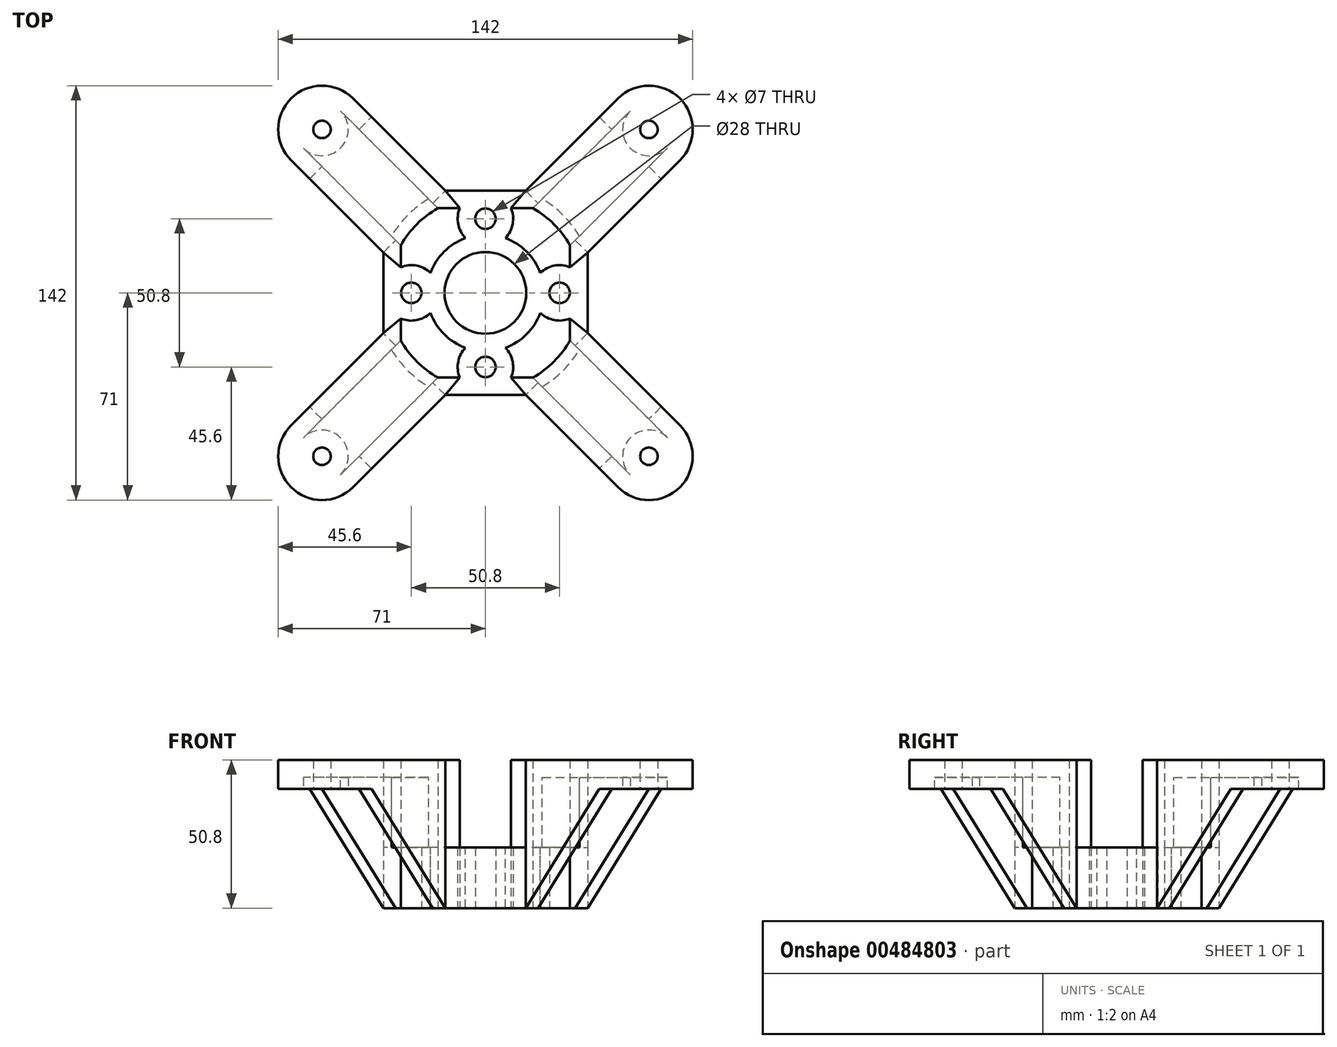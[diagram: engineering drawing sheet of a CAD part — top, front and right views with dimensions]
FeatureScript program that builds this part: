
annotation { "Feature Type Name" : "Feature", "Feature Type Description" : "" }
export const myFeature = defineFeature(function(context is Context, id is Id, definition is map)
    precondition{}
    {
        {
            var Q0;
            Q0=qCreatedBy(makeId("Top.planeOp"),FACE);
            var sketch = newSketch(context, id + "F0", { "sketchPlane" : qUnion([Q0])});
            skCircle(sketch, "E0", {"center": v(0, 0) * mm, "radius": 14 * mm});
            skCircle(sketch, "E1", {"center": v(0, 0) * mm, "radius": 25.4 * mm});
            skLineSegment(sketch, "E2", {"start": v(0, 0) * mm, "end": v(0, 25.4) * mm, "construction": true});
            skLineSegment(sketch, "E3", {"start": v(0, 0) * mm, "end": v(0, -25.4) * mm, "construction": true});
            skCircle(sketch, "E4", {"center": v(0, 25.4) * mm, "radius": 3.5 * mm});
            skLineSegment(sketch, "E5", {"start": v(0, 0) * mm, "end": v(25.4, 0) * mm, "construction": true});
            skCircle(sketch, "E6.MirrorC", {"center": v(0, -25.4) * mm, "radius": 3.5 * mm});
            skLineSegment(sketch, "E7.bottom", {"start": v(-35, 35) * mm, "end": v(35, 35) * mm});
            skLineSegment(sketch, "E7.top", {"start": v(-35, -35) * mm, "end": v(35, -35) * mm});
            skLineSegment(sketch, "E7.left", {"start": v(-35, 35) * mm, "end": v(-35, -35) * mm});
            skLineSegment(sketch, "E7.right", {"start": v(35, 35) * mm, "end": v(35, -35) * mm});
            skCircle(sketch, "E8", {"center": v(25.4, 0) * mm, "radius": 3.5 * mm});
            skCircle(sketch, "E9.MirrorC", {"center": v(-25.4, 0) * mm, "radius": 3.5 * mm});
            skLineSegment(sketch, "E10.bottom", {"start": v(-56, -56) * mm, "end": v(56, -56) * mm, "construction": true});
            skLineSegment(sketch, "E10.top", {"start": v(-56, 56) * mm, "end": v(56, 56) * mm, "construction": true});
            skLineSegment(sketch, "E10.left", {"start": v(-56, -56) * mm, "end": v(-56, 56) * mm, "construction": true});
            skLineSegment(sketch, "E10.right", {"start": v(56, -56) * mm, "end": v(56, 56) * mm, "construction": true});
            skLineSegment(sketch, "E11", {"start": v(0, 0) * mm, "end": v(-56, 56) * mm, "construction": true});
            skLineSegment(sketch, "E12.0", {"start": v(-13.79, 35) * mm, "end": v(-45.4, 66.6) * mm});
            skLineSegment(sketch, "E13.0", {"start": v(-35, 13.79) * mm, "end": v(-66.6, 45.4) * mm});
            skArc(sketch, "E14", {"start": v(-45.4, 66.6) * mm, "mid": v(-66.6, 66.6) * mm, "end": v(-66.6, 45.4) * mm});
            skCircle(sketch, "E15", {"center": v(-56, 56) * mm, "radius": 3 * mm});
            skLineSegment(sketch, "E16.MirrorCS", {"start": v(13.79, 35) * mm, "end": v(45.4, 66.6) * mm});
            skArc(sketch, "E17.MirrorCS", {"start": v(45.4, 66.6) * mm, "mid": v(66.6, 66.6) * mm, "end": v(66.6, 45.4) * mm});
            skLineSegment(sketch, "E18.MirrorCS", {"start": v(35, 13.79) * mm, "end": v(66.6, 45.4) * mm});
            skCircle(sketch, "E19.MirrorC", {"center": v(56, 56) * mm, "radius": 3 * mm});
            skLineSegment(sketch, "E20.MirrorCS", {"start": v(-13.79, -35) * mm, "end": v(-45.4, -66.6) * mm});
            skArc(sketch, "E21.MirrorCS", {"start": v(-45.4, -66.6) * mm, "mid": v(-66.6, -66.6) * mm, "end": v(-66.6, -45.4) * mm});
            skLineSegment(sketch, "E22.MirrorCS", {"start": v(-35, -13.79) * mm, "end": v(-66.6, -45.4) * mm});
            skCircle(sketch, "E23.MirrorC", {"center": v(-56, -56) * mm, "radius": 3 * mm});
            skCircle(sketch, "E24.MirrorC", {"center": v(56, -56) * mm, "radius": 3 * mm});
            skArc(sketch, "E25.MirrorCS", {"start": v(45.4, -66.6) * mm, "mid": v(66.6, -66.6) * mm, "end": v(66.6, -45.4) * mm});
            skLineSegment(sketch, "E26.MirrorCS", {"start": v(13.79, -35) * mm, "end": v(45.4, -66.6) * mm});
            skLineSegment(sketch, "E27.MirrorCS", {"start": v(35, -13.79) * mm, "end": v(66.6, -45.4) * mm});
            skSolve(sketch);
        }
        {
            var Q0;
            Q0 = qSketchRegion(id + "F0", true);
            var Q1;
            Q1=makeQuery(id+"F0.imprint","IMPRINT",FACE,{"disambiguationData":[TD([[makeQuery(id+"F0.imprint","IMPRINT",EDGE,{"derivedFrom":sQuery(id+"F0.wireOp",EDGE,"E0")}),-1.0]])]});
            extrude(context, id + "F1", {"entities" : qUnion([Q0, Q1]), "depth" : 50.8 * mm});
        }
        {
            var Q0;
            Q0=makeQuery(id+"F1.opExtrude","CAP_FACE",FACE,{"disambiguationData":[OSD([sQuery(id+"F0.wireOp",EDGE,"E0"),sQuery(id+"F0.wireOp",EDGE,"E4"),sQuery(id+"F0.wireOp",EDGE,"E6.MirrorC"),sQuery(id+"F0.wireOp",EDGE,"E7.bottom"),sQuery(id+"F0.wireOp",EDGE,"E7.top"),sQuery(id+"F0.wireOp",EDGE,"E7.left"),sQuery(id+"F0.wireOp",EDGE,"E7.right"),sQuery(id+"F0.wireOp",EDGE,"E8"),sQuery(id+"F0.wireOp",EDGE,"E9.MirrorC"),sQuery(id+"F0.wireOp",EDGE,"E12.0"),sQuery(id+"F0.wireOp",EDGE,"E13.0"),sQuery(id+"F0.wireOp",EDGE,"E14"),sQuery(id+"F0.wireOp",EDGE,"E15"),sQuery(id+"F0.wireOp",EDGE,"E16.MirrorCS"),sQuery(id+"F0.wireOp",EDGE,"E17.MirrorCS"),sQuery(id+"F0.wireOp",EDGE,"E18.MirrorCS"),sQuery(id+"F0.wireOp",EDGE,"E19.MirrorC"),sQuery(id+"F0.wireOp",EDGE,"E20.MirrorCS"),sQuery(id+"F0.wireOp",EDGE,"E21.MirrorCS"),sQuery(id+"F0.wireOp",EDGE,"E22.MirrorCS"),sQuery(id+"F0.wireOp",EDGE,"E23.MirrorC"),sQuery(id+"F0.wireOp",EDGE,"E24.MirrorC"),sQuery(id+"F0.wireOp",EDGE,"E25.MirrorCS"),sQuery(id+"F0.wireOp",EDGE,"E26.MirrorCS"),sQuery(id+"F0.wireOp",EDGE,"E27.MirrorCS")])],"isStart":true});
            shell(context, id + "F2", {"entities" : qUnion([Q0]), "thickness" : 6 * mm});
        }
        {
            var Q0;
            Q0=makeQuery(id+"F1.opExtrude","SWEPT_FACE",FACE,{"disambiguationData":[OSD([sQuery(id+"F0.wireOp",EDGE,"E26.MirrorCS")])]});
            var sketch = newSketch(context, id + "F3", { "sketchPlane" : qUnion([Q0])});
            skLineSegment(sketch, "E28", {"start": v(94.2, 40.8) * mm, "end": v(94.2, 40.8) * mm});
            skLineSegment(sketch, "E29", {"start": v(94.2, 40.8) * mm, "end": v(34.5, 40.8) * mm});
            skLineSegment(sketch, "E30", {"start": v(34.5, 40.8) * mm, "end": v(34.5, 0) * mm});
            skPoint(sketch, "E31.0", {"position": v(94.2, 0) * mm});
            skPoint(sketch, "E32.0", {"position": v(94.2, 50.8) * mm});
            skLineSegment(sketch, "E33", {"start": v(34.5, 0) * mm, "end": v(94.2, 0) * mm});
            skPoint(sketch, "E34.0", {"position": v(70.2, 0) * mm});
            skLineSegment(sketch, "E35", {"start": v(70.2, 0) * mm, "end": v(70.2, 40.8) * mm});
            skLineSegment(sketch, "E36", {"start": v(70.2, 40.8) * mm, "end": v(34.5, 0) * mm});
            skLineSegment(sketch, "E37", {"start": v(94.2, 0) * mm, "end": v(94.2, 40.8) * mm});
            skSolve(sketch);
        }
        {
            var Q0;
            {var subQ0=sQuery(id+"F3.wireOp",EDGE,"E37");Q0=makeQuery(id+"F3.imprint","IMPRINT",FACE,{"disambiguationData":[TD([[makeQuery(id+"F3.imprint","IMPRINT",EDGE,{"derivedFrom":subQ0}),1.0]])]});}
            var Q1;
            {var subQ0=sQuery(id+"F3.wireOp",EDGE,"E35");Q1=makeQuery(id+"F3.imprint","IMPRINT",FACE,{"disambiguationData":[TD([[makeQuery(id+"F3.imprint","IMPRINT",EDGE,{"derivedFrom":subQ0}),-1.0]])]});}
            var Q2;
            {var subQ2=sQuery(id+"F3.wireOp",EDGE,"E35");Q2=makeQuery(id+"F3.imprint","IMPRINT",FACE,{"disambiguationData":[TD([[makeQuery(id+"F3.imprint","IMPRINT",EDGE,{"derivedFrom":subQ2}),1.0]])]});}
            extrude(context, id + "F4", {"entities" : qUnion([Q0, Q1, Q2]), "operationType" : NewBodyOperationType.REMOVE, "endBound" : BoundingType.THROUGH_ALL, "oppositeDirection" : true, "depth" : 25.4 * mm});
        }
        {
            var Q0;
            Q0=makeQuery(id+"F1.opExtrude","SWEPT_FACE",FACE,{"disambiguationData":[OSD([sQuery(id+"F0.wireOp",EDGE,"E18.MirrorCS")])]});
            var sketch = newSketch(context, id + "F5", { "sketchPlane" : qUnion([Q0])});
            skPoint(sketch, "E38.0", {"position": v(94.2, 0) * mm});
            skPoint(sketch, "E39.0", {"position": v(70.2, 0) * mm});
            skPoint(sketch, "E40.0", {"position": v(94.2, 50.8) * mm});
            skLineSegment(sketch, "E41", {"start": v(94.2, 0) * mm, "end": v(94.2, 40.8) * mm});
            skLineSegment(sketch, "E42", {"start": v(94.2, 0) * mm, "end": v(34.5, 0) * mm});
            skLineSegment(sketch, "E43", {"start": v(70.2, 0) * mm, "end": v(70.2, 40.8) * mm});
            skLineSegment(sketch, "E44", {"start": v(94.2, 40.8) * mm, "end": v(34.5, 40.8) * mm});
            skLineSegment(sketch, "E45", {"start": v(34.5, 40.8) * mm, "end": v(34.5, 0) * mm});
            skLineSegment(sketch, "E46", {"start": v(70.2, 40.8) * mm, "end": v(34.5, 0) * mm});
            skSolve(sketch);
        }
        {
            var Q0;
            {var subQ0=sQuery(id+"F5.wireOp",EDGE,"E41");Q0=makeQuery(id+"F5.imprint","IMPRINT",FACE,{"disambiguationData":[TD([[makeQuery(id+"F5.imprint","IMPRINT",EDGE,{"derivedFrom":subQ0}),1.0]])]});}
            var Q1;
            {var subQ3=sQuery(id+"F5.wireOp",EDGE,"E43");Q1=makeQuery(id+"F5.imprint","IMPRINT",FACE,{"disambiguationData":[TD([[makeQuery(id+"F5.imprint","IMPRINT",EDGE,{"derivedFrom":subQ3}),-1.0]])]});}
            var Q2;
            {var subQ2=sQuery(id+"F5.wireOp",EDGE,"E43");Q2=makeQuery(id+"F5.imprint","IMPRINT",FACE,{"disambiguationData":[TD([[makeQuery(id+"F5.imprint","IMPRINT",EDGE,{"derivedFrom":subQ2}),1.0]])]});}
            extrude(context, id + "F6", {"entities" : qUnion([Q0, Q1, Q2]), "operationType" : NewBodyOperationType.REMOVE, "endBound" : BoundingType.THROUGH_ALL, "oppositeDirection" : true, "depth" : 25.4 * mm});
        }
        {
            var Q0;
            Q0=makeQuery(id+"F1.opExtrude","SWEPT_FACE",FACE,{"disambiguationData":[OSD([sQuery(id+"F0.wireOp",EDGE,"E12.0")])]});
            var sketch = newSketch(context, id + "F7", { "sketchPlane" : qUnion([Q0])});
            skPoint(sketch, "E47.0", {"position": v(94.2, 0) * mm});
            skPoint(sketch, "E48.0", {"position": v(94.2, 50.8) * mm});
            skPoint(sketch, "E49.0", {"position": v(70.2, 0) * mm});
            skLineSegment(sketch, "E50", {"start": v(94.2, 0) * mm, "end": v(34.5, 0) * mm});
            skLineSegment(sketch, "E51", {"start": v(34.5, 0) * mm, "end": v(34.5, 40.8) * mm});
            skLineSegment(sketch, "E52", {"start": v(94.2, 0) * mm, "end": v(94.2, 40.8) * mm});
            skLineSegment(sketch, "E53", {"start": v(94.2, 40.8) * mm, "end": v(34.5, 40.8) * mm});
            skLineSegment(sketch, "E54", {"start": v(70.2, 0) * mm, "end": v(70.2, 40.8) * mm});
            skLineSegment(sketch, "E55", {"start": v(70.2, 40.8) * mm, "end": v(34.5, 0) * mm});
            skSolve(sketch);
        }
        {
            var Q0;
            {var subQ3=sQuery(id+"F7.wireOp",EDGE,"E52");Q0=makeQuery(id+"F7.imprint","IMPRINT",FACE,{"disambiguationData":[TD([[makeQuery(id+"F7.imprint","IMPRINT",EDGE,{"derivedFrom":subQ3}),1.0]])]});}
            var Q1;
            {var subQ3=sQuery(id+"F7.wireOp",EDGE,"E54");Q1=makeQuery(id+"F7.imprint","IMPRINT",FACE,{"disambiguationData":[TD([[makeQuery(id+"F7.imprint","IMPRINT",EDGE,{"derivedFrom":subQ3}),-1.0]])]});}
            var Q2;
            {var subQ2=sQuery(id+"F7.wireOp",EDGE,"E54");Q2=makeQuery(id+"F7.imprint","IMPRINT",FACE,{"disambiguationData":[TD([[makeQuery(id+"F7.imprint","IMPRINT",EDGE,{"derivedFrom":subQ2}),1.0]])]});}
            extrude(context, id + "F8", {"entities" : qUnion([Q0, Q1, Q2]), "operationType" : NewBodyOperationType.REMOVE, "endBound" : BoundingType.THROUGH_ALL, "oppositeDirection" : true, "depth" : 25.4 * mm});
        }
        {
            var Q0;
            Q0=makeQuery(id+"F1.opExtrude","SWEPT_FACE",FACE,{"disambiguationData":[OSD([sQuery(id+"F0.wireOp",EDGE,"E22.MirrorCS")])]});
            var sketch = newSketch(context, id + "F9", { "sketchPlane" : qUnion([Q0])});
            skPoint(sketch, "E56.0", {"position": v(94.2, 0) * mm});
            skPoint(sketch, "E56.1", {"position": v(70.2, 0) * mm});
            skPoint(sketch, "E56.2", {"position": v(94.2, 50.8) * mm});
            skLineSegment(sketch, "E57", {"start": v(94.2, 0) * mm, "end": v(34.5, 0) * mm});
            skLineSegment(sketch, "E58", {"start": v(34.5, 0) * mm, "end": v(34.5, 40.8) * mm});
            skLineSegment(sketch, "E59", {"start": v(94.2, 0) * mm, "end": v(94.2, 40.8) * mm});
            skLineSegment(sketch, "E60", {"start": v(94.2, 40.8) * mm, "end": v(34.5, 40.8) * mm});
            skLineSegment(sketch, "E61", {"start": v(70.2, 0) * mm, "end": v(70.2, 40.8) * mm});
            skLineSegment(sketch, "E62", {"start": v(70.2, 40.8) * mm, "end": v(34.5, 0) * mm});
            skSolve(sketch);
        }
        {
            var Q0;
            {var subQ2=sQuery(id+"F9.wireOp",EDGE,"E61");Q0=makeQuery(id+"F9.imprint","IMPRINT",FACE,{"disambiguationData":[TD([[makeQuery(id+"F9.imprint","IMPRINT",EDGE,{"derivedFrom":subQ2}),1.0]])]});}
            var Q1;
            {var subQ3=sQuery(id+"F9.wireOp",EDGE,"E61");Q1=makeQuery(id+"F9.imprint","IMPRINT",FACE,{"disambiguationData":[TD([[makeQuery(id+"F9.imprint","IMPRINT",EDGE,{"derivedFrom":subQ3}),-1.0]])]});}
            var Q2;
            {var subQ3=sQuery(id+"F9.wireOp",EDGE,"E59");Q2=makeQuery(id+"F9.imprint","IMPRINT",FACE,{"disambiguationData":[TD([[makeQuery(id+"F9.imprint","IMPRINT",EDGE,{"derivedFrom":subQ3}),1.0]])]});}
            extrude(context, id + "F10", {"entities" : qUnion([Q0, Q1, Q2]), "operationType" : NewBodyOperationType.REMOVE, "endBound" : BoundingType.THROUGH_ALL, "oppositeDirection" : true, "depth" : 25.4 * mm});
        }
        {
            var Q0;
            Q0=makeQuery(id+"F1.opExtrude","CAP_FACE",FACE,{"disambiguationData":[OSD([sQuery(id+"F0.wireOp",EDGE,"E0"),sQuery(id+"F0.wireOp",EDGE,"E4"),sQuery(id+"F0.wireOp",EDGE,"E6.MirrorC"),sQuery(id+"F0.wireOp",EDGE,"E7.bottom"),sQuery(id+"F0.wireOp",EDGE,"E7.top"),sQuery(id+"F0.wireOp",EDGE,"E7.left"),sQuery(id+"F0.wireOp",EDGE,"E7.right"),sQuery(id+"F0.wireOp",EDGE,"E8"),sQuery(id+"F0.wireOp",EDGE,"E9.MirrorC"),sQuery(id+"F0.wireOp",EDGE,"E12.0"),sQuery(id+"F0.wireOp",EDGE,"E13.0"),sQuery(id+"F0.wireOp",EDGE,"E14"),sQuery(id+"F0.wireOp",EDGE,"E15"),sQuery(id+"F0.wireOp",EDGE,"E16.MirrorCS"),sQuery(id+"F0.wireOp",EDGE,"E17.MirrorCS"),sQuery(id+"F0.wireOp",EDGE,"E18.MirrorCS"),sQuery(id+"F0.wireOp",EDGE,"E19.MirrorC"),sQuery(id+"F0.wireOp",EDGE,"E20.MirrorCS"),sQuery(id+"F0.wireOp",EDGE,"E21.MirrorCS"),sQuery(id+"F0.wireOp",EDGE,"E22.MirrorCS"),sQuery(id+"F0.wireOp",EDGE,"E23.MirrorC"),sQuery(id+"F0.wireOp",EDGE,"E24.MirrorC"),sQuery(id+"F0.wireOp",EDGE,"E25.MirrorCS"),sQuery(id+"F0.wireOp",EDGE,"E26.MirrorCS"),sQuery(id+"F0.wireOp",EDGE,"E27.MirrorCS")])],"isStart":false});
            var sketch = newSketch(context, id + "F11", { "sketchPlane" : qUnion([Q0])});
            skLineSegment(sketch, "E63.bottom", {"start": v(35, 35) * mm, "end": v(-35, 35) * mm});
            skLineSegment(sketch, "E63.top", {"start": v(35, -35) * mm, "end": v(-35, -35) * mm});
            skLineSegment(sketch, "E63.left", {"start": v(35, 35) * mm, "end": v(35, -35) * mm});
            skLineSegment(sketch, "E63.right", {"start": v(-35, 35) * mm, "end": v(-35, -35) * mm});
            skPoint(sketch, "E63.middle", {"position": v(0, 0) * mm});
            skPoint(sketch, "E64.0", {"position": v(-13.79, 35) * mm});
            skPoint(sketch, "E65.0", {"position": v(13.79, 35) * mm});
            skPoint(sketch, "E66.0", {"position": v(35, 13.79) * mm});
            skPoint(sketch, "E67.0", {"position": v(35, -13.79) * mm});
            skPoint(sketch, "E68.0", {"position": v(-35, 13.79) * mm});
            skPoint(sketch, "E69.0", {"position": v(-35, -13.79) * mm});
            skPoint(sketch, "E70.0", {"position": v(-13.79, -35) * mm});
            skPoint(sketch, "E71.0", {"position": v(13.79, -35) * mm});
            skCircle(sketch, "E72", {"center": v(0, 0) * mm, "radius": 37.62 * mm});
            skSolve(sketch);
        }
        {
            var Q0;
            Q0=makeQuery(id+"F11.imprint","IMPRINT",FACE,{"disambiguationData":[TD([[makeQuery(id+"F11.imprint","IMPRINT",EDGE,{"derivedFrom":makeQuery(id+"F1.opExtrude","CAP_EDGE",EDGE,{"disambiguationData":[OSD([sQuery(id+"F0.wireOp",EDGE,"E0")])],"isStart":false})}),-1.0]])]});
            extrude(context, id + "F12", {"entities" : qUnion([Q0]), "operationType" : NewBodyOperationType.REMOVE, "oppositeDirection" : true, "depth" : 30 * mm});
        }
        {
            var Q0;
            Q0=makeQuery(id+"F12.boolean.opBoolean","COPY",FACE,{"derivedFrom":makeQuery(id+"F12.opExtrude","CAP_FACE",FACE,{"disambiguationData":[OSD([sQuery(id+"F0.wireOp",EDGE,"E0"),sQuery(id+"F0.wireOp",EDGE,"E4"),sQuery(id+"F0.wireOp",EDGE,"E6.MirrorC"),sQuery(id+"F0.wireOp",EDGE,"E8"),sQuery(id+"F0.wireOp",EDGE,"E9.MirrorC"),sQuery(id+"F11.wireOp",EDGE,"E63.bottom"),sQuery(id+"F11.wireOp",EDGE,"E63.top"),sQuery(id+"F11.wireOp",EDGE,"E63.left"),sQuery(id+"F11.wireOp",EDGE,"E63.right"),sQuery(id+"F11.wireOp",EDGE,"E72")])],"isStart":false})});
            var sketch = newSketch(context, id + "F13", { "sketchPlane" : qUnion([Q0])});
            skCircle(sketch, "E73", {"center": v(0, 0) * mm, "radius": 37.62 * mm});
            skCircle(sketch, "E74", {"center": v(0, 0) * mm, "radius": 33.25 * mm});
            skLineSegment(sketch, "E75", {"start": v(-13.79, 35) * mm, "end": v(-8.8, 29) * mm});
            skLineSegment(sketch, "E76", {"start": v(8.8, 29) * mm, "end": v(13.79, 35) * mm});
            skLineSegment(sketch, "E77", {"start": v(-29, 8.8) * mm, "end": v(-35, 13.79) * mm});
            skLineSegment(sketch, "E78", {"start": v(29, 8.8) * mm, "end": v(35, 13.79) * mm});
            skLineSegment(sketch, "E79", {"start": v(29, -8.8) * mm, "end": v(35, -13.79) * mm});
            skLineSegment(sketch, "E80", {"start": v(8.8, -29) * mm, "end": v(13.79, -35) * mm});
            skLineSegment(sketch, "E81", {"start": v(-8.8, -29) * mm, "end": v(-13.79, -35) * mm});
            skLineSegment(sketch, "E82", {"start": v(-29, -8.8) * mm, "end": v(-35, -13.79) * mm});
            skSolve(sketch);
        }
        {
            var Q0;
            {var subQ1=makeQuery(id+"F12.opExtrude","CAP_FACE",FACE,{"disambiguationData":[OSD([sQuery(id+"F0.wireOp",EDGE,"E0"),sQuery(id+"F0.wireOp",EDGE,"E4"),sQuery(id+"F0.wireOp",EDGE,"E6.MirrorC"),sQuery(id+"F0.wireOp",EDGE,"E8"),sQuery(id+"F0.wireOp",EDGE,"E9.MirrorC"),sQuery(id+"F11.wireOp",EDGE,"E63.bottom"),sQuery(id+"F11.wireOp",EDGE,"E63.top"),sQuery(id+"F11.wireOp",EDGE,"E63.left"),sQuery(id+"F11.wireOp",EDGE,"E63.right"),sQuery(id+"F11.wireOp",EDGE,"E72")])],"isStart":false});var subQ2=makeQuery(id+"F12.boolean.opBoolean","INTERSECT",EDGE,{"derivedFrom":[makeQuery(id+"F2.opShell","OFFSET_FACE",FACE,{"disambiguationData":[OSD([sQuery(id+"F0.wireOp",EDGE,"E26.MirrorCS")])]}),subQ1]});Q0=makeQuery(id+"F13.imprint","IMPRINT",FACE,{"disambiguationData":[TD([[makeQuery(id+"F13.imprint","IMPRINT",EDGE,{"derivedFrom":subQ2}),1.0]])]});}
            var Q1;
            {var subQ0=sQuery(id+"F13.wireOp",EDGE,"E80");var subQ6=sQuery(id+"F13.wireOp",EDGE,"E74");var subQ7=makeQuery(id+"F13.imprint","INTERSECT",VERTEX,{"derivedFrom":[subQ6,subQ0]});Q1=makeQuery(id+"F13.imprint","IMPRINT",FACE,{"disambiguationData":[TD([[makeQuery(id+"F13.imprint","IMPRINT",EDGE,{"disambiguationData":[TD([[subQ7,-1.0]])],"derivedFrom":subQ0}),1.0]])]});}
            var Q2;
            {var subQ0=sQuery(id+"F13.wireOp",EDGE,"E79");var subQ6=sQuery(id+"F13.wireOp",EDGE,"E74");var subQ7=makeQuery(id+"F13.imprint","INTERSECT",VERTEX,{"derivedFrom":[subQ6,subQ0]});Q2=makeQuery(id+"F13.imprint","IMPRINT",FACE,{"disambiguationData":[TD([[makeQuery(id+"F13.imprint","IMPRINT",EDGE,{"disambiguationData":[TD([[subQ7,-1.0]])],"derivedFrom":subQ0}),-1.0]])]});}
            var Q3;
            {var subQ0=sQuery(id+"F13.wireOp",EDGE,"E81");var subQ6=sQuery(id+"F13.wireOp",EDGE,"E74");var subQ7=makeQuery(id+"F13.imprint","INTERSECT",VERTEX,{"derivedFrom":[subQ6,subQ0]});Q3=makeQuery(id+"F13.imprint","IMPRINT",FACE,{"disambiguationData":[TD([[makeQuery(id+"F13.imprint","IMPRINT",EDGE,{"disambiguationData":[TD([[subQ7,-1.0]])],"derivedFrom":subQ0}),-1.0]])]});}
            var Q4;
            {var subQ1=makeQuery(id+"F12.opExtrude","CAP_FACE",FACE,{"disambiguationData":[OSD([sQuery(id+"F0.wireOp",EDGE,"E0"),sQuery(id+"F0.wireOp",EDGE,"E4"),sQuery(id+"F0.wireOp",EDGE,"E6.MirrorC"),sQuery(id+"F0.wireOp",EDGE,"E8"),sQuery(id+"F0.wireOp",EDGE,"E9.MirrorC"),sQuery(id+"F11.wireOp",EDGE,"E63.bottom"),sQuery(id+"F11.wireOp",EDGE,"E63.top"),sQuery(id+"F11.wireOp",EDGE,"E63.left"),sQuery(id+"F11.wireOp",EDGE,"E63.right"),sQuery(id+"F11.wireOp",EDGE,"E72")])],"isStart":false});var subQ2=makeQuery(id+"F12.boolean.opBoolean","INTERSECT",EDGE,{"derivedFrom":[makeQuery(id+"F2.opShell","OFFSET_FACE",FACE,{"disambiguationData":[OSD([sQuery(id+"F0.wireOp",EDGE,"E20.MirrorCS")])]}),subQ1]});Q4=makeQuery(id+"F13.imprint","IMPRINT",FACE,{"disambiguationData":[TD([[makeQuery(id+"F13.imprint","IMPRINT",EDGE,{"derivedFrom":subQ2}),-1.0]])]});}
            var Q5;
            {var subQ0=sQuery(id+"F13.wireOp",EDGE,"E82");var subQ6=sQuery(id+"F13.wireOp",EDGE,"E74");var subQ7=makeQuery(id+"F13.imprint","INTERSECT",VERTEX,{"derivedFrom":[subQ6,subQ0]});Q5=makeQuery(id+"F13.imprint","IMPRINT",FACE,{"disambiguationData":[TD([[makeQuery(id+"F13.imprint","IMPRINT",EDGE,{"disambiguationData":[TD([[subQ7,-1.0]])],"derivedFrom":subQ0}),1.0]])]});}
            var Q6;
            {var subQ1=sQuery(id+"F0.wireOp",EDGE,"E8");var subQ2=makeQuery(id+"F12.opExtrude","CAP_FACE",FACE,{"disambiguationData":[OSD([sQuery(id+"F0.wireOp",EDGE,"E0"),sQuery(id+"F0.wireOp",EDGE,"E4"),sQuery(id+"F0.wireOp",EDGE,"E6.MirrorC"),subQ1,sQuery(id+"F0.wireOp",EDGE,"E9.MirrorC"),sQuery(id+"F11.wireOp",EDGE,"E63.bottom"),sQuery(id+"F11.wireOp",EDGE,"E63.top"),sQuery(id+"F11.wireOp",EDGE,"E63.left"),sQuery(id+"F11.wireOp",EDGE,"E63.right"),sQuery(id+"F11.wireOp",EDGE,"E72")])],"isStart":false});var subQ3=makeQuery(id+"F12.boolean.opBoolean","INTERSECT",EDGE,{"derivedFrom":[makeQuery(id+"F2.opShell","OFFSET_FACE",FACE,{"disambiguationData":[OSD([sQuery(id+"F0.wireOp",EDGE,"E7.right")]),OD(1.0)]}),subQ2]});Q6=makeQuery(id+"F13.imprint","IMPRINT",FACE,{"disambiguationData":[TD([[makeQuery(id+"F13.imprint","IMPRINT",EDGE,{"derivedFrom":subQ3}),1.0]])]});}
            var Q7;
            {var subQ1=sQuery(id+"F0.wireOp",EDGE,"E6.MirrorC");var subQ2=makeQuery(id+"F12.opExtrude","CAP_FACE",FACE,{"disambiguationData":[OSD([sQuery(id+"F0.wireOp",EDGE,"E0"),sQuery(id+"F0.wireOp",EDGE,"E4"),subQ1,sQuery(id+"F0.wireOp",EDGE,"E8"),sQuery(id+"F0.wireOp",EDGE,"E9.MirrorC"),sQuery(id+"F11.wireOp",EDGE,"E63.bottom"),sQuery(id+"F11.wireOp",EDGE,"E63.top"),sQuery(id+"F11.wireOp",EDGE,"E63.left"),sQuery(id+"F11.wireOp",EDGE,"E63.right"),sQuery(id+"F11.wireOp",EDGE,"E72")])],"isStart":false});var subQ3=makeQuery(id+"F12.boolean.opBoolean","INTERSECT",EDGE,{"derivedFrom":[makeQuery(id+"F2.opShell","OFFSET_FACE",FACE,{"disambiguationData":[OSD([sQuery(id+"F0.wireOp",EDGE,"E7.top")]),OD(1.0)]}),subQ2]});Q7=makeQuery(id+"F13.imprint","IMPRINT",FACE,{"disambiguationData":[TD([[makeQuery(id+"F13.imprint","IMPRINT",EDGE,{"derivedFrom":subQ3}),-1.0]])]});}
            var Q8;
            {var subQ1=sQuery(id+"F0.wireOp",EDGE,"E6.MirrorC");var subQ2=makeQuery(id+"F12.opExtrude","CAP_FACE",FACE,{"disambiguationData":[OSD([sQuery(id+"F0.wireOp",EDGE,"E0"),sQuery(id+"F0.wireOp",EDGE,"E4"),subQ1,sQuery(id+"F0.wireOp",EDGE,"E8"),sQuery(id+"F0.wireOp",EDGE,"E9.MirrorC"),sQuery(id+"F11.wireOp",EDGE,"E63.bottom"),sQuery(id+"F11.wireOp",EDGE,"E63.top"),sQuery(id+"F11.wireOp",EDGE,"E63.left"),sQuery(id+"F11.wireOp",EDGE,"E63.right"),sQuery(id+"F11.wireOp",EDGE,"E72")])],"isStart":false});var subQ3=makeQuery(id+"F12.boolean.opBoolean","INTERSECT",EDGE,{"derivedFrom":[makeQuery(id+"F2.opShell","OFFSET_FACE",FACE,{"disambiguationData":[OSD([sQuery(id+"F0.wireOp",EDGE,"E7.top")]),OD(0.0)]}),subQ2]});Q8=makeQuery(id+"F13.imprint","IMPRINT",FACE,{"disambiguationData":[TD([[makeQuery(id+"F13.imprint","IMPRINT",EDGE,{"derivedFrom":subQ3}),-1.0]])]});}
            var Q9;
            {var subQ1=sQuery(id+"F0.wireOp",EDGE,"E9.MirrorC");var subQ2=makeQuery(id+"F12.opExtrude","CAP_FACE",FACE,{"disambiguationData":[OSD([sQuery(id+"F0.wireOp",EDGE,"E0"),sQuery(id+"F0.wireOp",EDGE,"E4"),sQuery(id+"F0.wireOp",EDGE,"E6.MirrorC"),sQuery(id+"F0.wireOp",EDGE,"E8"),subQ1,sQuery(id+"F11.wireOp",EDGE,"E63.bottom"),sQuery(id+"F11.wireOp",EDGE,"E63.top"),sQuery(id+"F11.wireOp",EDGE,"E63.left"),sQuery(id+"F11.wireOp",EDGE,"E63.right"),sQuery(id+"F11.wireOp",EDGE,"E72")])],"isStart":false});var subQ3=makeQuery(id+"F12.boolean.opBoolean","INTERSECT",EDGE,{"derivedFrom":[makeQuery(id+"F2.opShell","OFFSET_FACE",FACE,{"disambiguationData":[OSD([sQuery(id+"F0.wireOp",EDGE,"E7.left")]),OD(1.0)]}),subQ2]});Q9=makeQuery(id+"F13.imprint","IMPRINT",FACE,{"disambiguationData":[TD([[makeQuery(id+"F13.imprint","IMPRINT",EDGE,{"derivedFrom":subQ3}),-1.0]])]});}
            var Q10;
            {var subQ1=sQuery(id+"F0.wireOp",EDGE,"E9.MirrorC");var subQ2=makeQuery(id+"F12.opExtrude","CAP_FACE",FACE,{"disambiguationData":[OSD([sQuery(id+"F0.wireOp",EDGE,"E0"),sQuery(id+"F0.wireOp",EDGE,"E4"),sQuery(id+"F0.wireOp",EDGE,"E6.MirrorC"),sQuery(id+"F0.wireOp",EDGE,"E8"),subQ1,sQuery(id+"F11.wireOp",EDGE,"E63.bottom"),sQuery(id+"F11.wireOp",EDGE,"E63.top"),sQuery(id+"F11.wireOp",EDGE,"E63.left"),sQuery(id+"F11.wireOp",EDGE,"E63.right"),sQuery(id+"F11.wireOp",EDGE,"E72")])],"isStart":false});var subQ3=makeQuery(id+"F12.boolean.opBoolean","INTERSECT",EDGE,{"derivedFrom":[makeQuery(id+"F2.opShell","OFFSET_FACE",FACE,{"disambiguationData":[OSD([sQuery(id+"F0.wireOp",EDGE,"E7.left")]),OD(0.0)]}),subQ2]});Q10=makeQuery(id+"F13.imprint","IMPRINT",FACE,{"disambiguationData":[TD([[makeQuery(id+"F13.imprint","IMPRINT",EDGE,{"derivedFrom":subQ3}),-1.0]])]});}
            var Q11;
            {var subQ0=sQuery(id+"F13.wireOp",EDGE,"E77");var subQ6=sQuery(id+"F13.wireOp",EDGE,"E74");var subQ7=makeQuery(id+"F13.imprint","INTERSECT",VERTEX,{"derivedFrom":[subQ6,subQ0]});Q11=makeQuery(id+"F13.imprint","IMPRINT",FACE,{"disambiguationData":[TD([[makeQuery(id+"F13.imprint","IMPRINT",EDGE,{"disambiguationData":[TD([[subQ7,-1.0]])],"derivedFrom":subQ0}),-1.0]])]});}
            var Q12;
            {var subQ1=makeQuery(id+"F12.opExtrude","CAP_FACE",FACE,{"disambiguationData":[OSD([sQuery(id+"F0.wireOp",EDGE,"E0"),sQuery(id+"F0.wireOp",EDGE,"E4"),sQuery(id+"F0.wireOp",EDGE,"E6.MirrorC"),sQuery(id+"F0.wireOp",EDGE,"E8"),sQuery(id+"F0.wireOp",EDGE,"E9.MirrorC"),sQuery(id+"F11.wireOp",EDGE,"E63.bottom"),sQuery(id+"F11.wireOp",EDGE,"E63.top"),sQuery(id+"F11.wireOp",EDGE,"E63.left"),sQuery(id+"F11.wireOp",EDGE,"E63.right"),sQuery(id+"F11.wireOp",EDGE,"E72")])],"isStart":false});var subQ2=makeQuery(id+"F12.boolean.opBoolean","INTERSECT",EDGE,{"derivedFrom":[makeQuery(id+"F2.opShell","OFFSET_FACE",FACE,{"disambiguationData":[OSD([sQuery(id+"F0.wireOp",EDGE,"E12.0")])]}),subQ1]});Q12=makeQuery(id+"F13.imprint","IMPRINT",FACE,{"disambiguationData":[TD([[makeQuery(id+"F13.imprint","IMPRINT",EDGE,{"derivedFrom":subQ2}),1.0]])]});}
            var Q13;
            {var subQ0=sQuery(id+"F13.wireOp",EDGE,"E75");var subQ6=sQuery(id+"F13.wireOp",EDGE,"E74");var subQ7=makeQuery(id+"F13.imprint","INTERSECT",VERTEX,{"derivedFrom":[subQ6,subQ0]});Q13=makeQuery(id+"F13.imprint","IMPRINT",FACE,{"disambiguationData":[TD([[makeQuery(id+"F13.imprint","IMPRINT",EDGE,{"disambiguationData":[TD([[subQ7,1.0]])],"derivedFrom":subQ0}),-1.0]])]});}
            var Q14;
            {var subQ1=sQuery(id+"F0.wireOp",EDGE,"E4");var subQ2=makeQuery(id+"F12.opExtrude","CAP_FACE",FACE,{"disambiguationData":[OSD([sQuery(id+"F0.wireOp",EDGE,"E0"),subQ1,sQuery(id+"F0.wireOp",EDGE,"E6.MirrorC"),sQuery(id+"F0.wireOp",EDGE,"E8"),sQuery(id+"F0.wireOp",EDGE,"E9.MirrorC"),sQuery(id+"F11.wireOp",EDGE,"E63.bottom"),sQuery(id+"F11.wireOp",EDGE,"E63.top"),sQuery(id+"F11.wireOp",EDGE,"E63.left"),sQuery(id+"F11.wireOp",EDGE,"E63.right"),sQuery(id+"F11.wireOp",EDGE,"E72")])],"isStart":false});var subQ3=makeQuery(id+"F12.boolean.opBoolean","INTERSECT",EDGE,{"derivedFrom":[makeQuery(id+"F2.opShell","OFFSET_FACE",FACE,{"disambiguationData":[OSD([sQuery(id+"F0.wireOp",EDGE,"E7.bottom")]),OD(0.0)]}),subQ2]});Q14=makeQuery(id+"F13.imprint","IMPRINT",FACE,{"disambiguationData":[TD([[makeQuery(id+"F13.imprint","IMPRINT",EDGE,{"derivedFrom":subQ3}),1.0]])]});}
            var Q15;
            {var subQ1=sQuery(id+"F0.wireOp",EDGE,"E4");var subQ2=makeQuery(id+"F12.opExtrude","CAP_FACE",FACE,{"disambiguationData":[OSD([sQuery(id+"F0.wireOp",EDGE,"E0"),subQ1,sQuery(id+"F0.wireOp",EDGE,"E6.MirrorC"),sQuery(id+"F0.wireOp",EDGE,"E8"),sQuery(id+"F0.wireOp",EDGE,"E9.MirrorC"),sQuery(id+"F11.wireOp",EDGE,"E63.bottom"),sQuery(id+"F11.wireOp",EDGE,"E63.top"),sQuery(id+"F11.wireOp",EDGE,"E63.left"),sQuery(id+"F11.wireOp",EDGE,"E63.right"),sQuery(id+"F11.wireOp",EDGE,"E72")])],"isStart":false});var subQ3=makeQuery(id+"F12.boolean.opBoolean","INTERSECT",EDGE,{"derivedFrom":[makeQuery(id+"F2.opShell","OFFSET_FACE",FACE,{"disambiguationData":[OSD([sQuery(id+"F0.wireOp",EDGE,"E7.bottom")]),OD(1.0)]}),subQ2]});Q15=makeQuery(id+"F13.imprint","IMPRINT",FACE,{"disambiguationData":[TD([[makeQuery(id+"F13.imprint","IMPRINT",EDGE,{"derivedFrom":subQ3}),1.0]])]});}
            var Q16;
            {var subQ0=sQuery(id+"F13.wireOp",EDGE,"E76");var subQ6=sQuery(id+"F13.wireOp",EDGE,"E74");var subQ7=makeQuery(id+"F13.imprint","INTERSECT",VERTEX,{"derivedFrom":[subQ6,subQ0]});Q16=makeQuery(id+"F13.imprint","IMPRINT",FACE,{"disambiguationData":[TD([[makeQuery(id+"F13.imprint","IMPRINT",EDGE,{"disambiguationData":[TD([[subQ7,-1.0]])],"derivedFrom":subQ0}),-1.0]])]});}
            var Q17;
            {var subQ1=makeQuery(id+"F12.opExtrude","CAP_FACE",FACE,{"disambiguationData":[OSD([sQuery(id+"F0.wireOp",EDGE,"E0"),sQuery(id+"F0.wireOp",EDGE,"E4"),sQuery(id+"F0.wireOp",EDGE,"E6.MirrorC"),sQuery(id+"F0.wireOp",EDGE,"E8"),sQuery(id+"F0.wireOp",EDGE,"E9.MirrorC"),sQuery(id+"F11.wireOp",EDGE,"E63.bottom"),sQuery(id+"F11.wireOp",EDGE,"E63.top"),sQuery(id+"F11.wireOp",EDGE,"E63.left"),sQuery(id+"F11.wireOp",EDGE,"E63.right"),sQuery(id+"F11.wireOp",EDGE,"E72")])],"isStart":false});var subQ2=makeQuery(id+"F12.boolean.opBoolean","INTERSECT",EDGE,{"derivedFrom":[makeQuery(id+"F2.opShell","OFFSET_FACE",FACE,{"disambiguationData":[OSD([sQuery(id+"F0.wireOp",EDGE,"E16.MirrorCS")])]}),subQ1]});Q17=makeQuery(id+"F13.imprint","IMPRINT",FACE,{"disambiguationData":[TD([[makeQuery(id+"F13.imprint","IMPRINT",EDGE,{"derivedFrom":subQ2}),-1.0]])]});}
            var Q18;
            {var subQ0=sQuery(id+"F13.wireOp",EDGE,"E78");var subQ6=sQuery(id+"F13.wireOp",EDGE,"E74");var subQ7=makeQuery(id+"F13.imprint","INTERSECT",VERTEX,{"derivedFrom":[subQ6,subQ0]});Q18=makeQuery(id+"F13.imprint","IMPRINT",FACE,{"disambiguationData":[TD([[makeQuery(id+"F13.imprint","IMPRINT",EDGE,{"disambiguationData":[TD([[subQ7,-1.0]])],"derivedFrom":subQ0}),1.0]])]});}
            var Q19;
            {var subQ1=sQuery(id+"F0.wireOp",EDGE,"E8");var subQ2=makeQuery(id+"F12.opExtrude","CAP_FACE",FACE,{"disambiguationData":[OSD([sQuery(id+"F0.wireOp",EDGE,"E0"),sQuery(id+"F0.wireOp",EDGE,"E4"),sQuery(id+"F0.wireOp",EDGE,"E6.MirrorC"),subQ1,sQuery(id+"F0.wireOp",EDGE,"E9.MirrorC"),sQuery(id+"F11.wireOp",EDGE,"E63.bottom"),sQuery(id+"F11.wireOp",EDGE,"E63.top"),sQuery(id+"F11.wireOp",EDGE,"E63.left"),sQuery(id+"F11.wireOp",EDGE,"E63.right"),sQuery(id+"F11.wireOp",EDGE,"E72")])],"isStart":false});var subQ3=makeQuery(id+"F12.boolean.opBoolean","INTERSECT",EDGE,{"derivedFrom":[makeQuery(id+"F2.opShell","OFFSET_FACE",FACE,{"disambiguationData":[OSD([sQuery(id+"F0.wireOp",EDGE,"E7.right")]),OD(0.0)]}),subQ2]});Q19=makeQuery(id+"F13.imprint","IMPRINT",FACE,{"disambiguationData":[TD([[makeQuery(id+"F13.imprint","IMPRINT",EDGE,{"derivedFrom":subQ3}),1.0]])]});}
            extrude(context, id + "F14", {"entities" : qUnion([Q0, Q1, Q2, Q3, Q4, Q5, Q6, Q7, Q8, Q9, Q10, Q11, Q12, Q13, Q14, Q15, Q16, Q17, Q18, Q19]), "operationType" : NewBodyOperationType.ADD, "depth" : 30 * mm});
        }
    });
